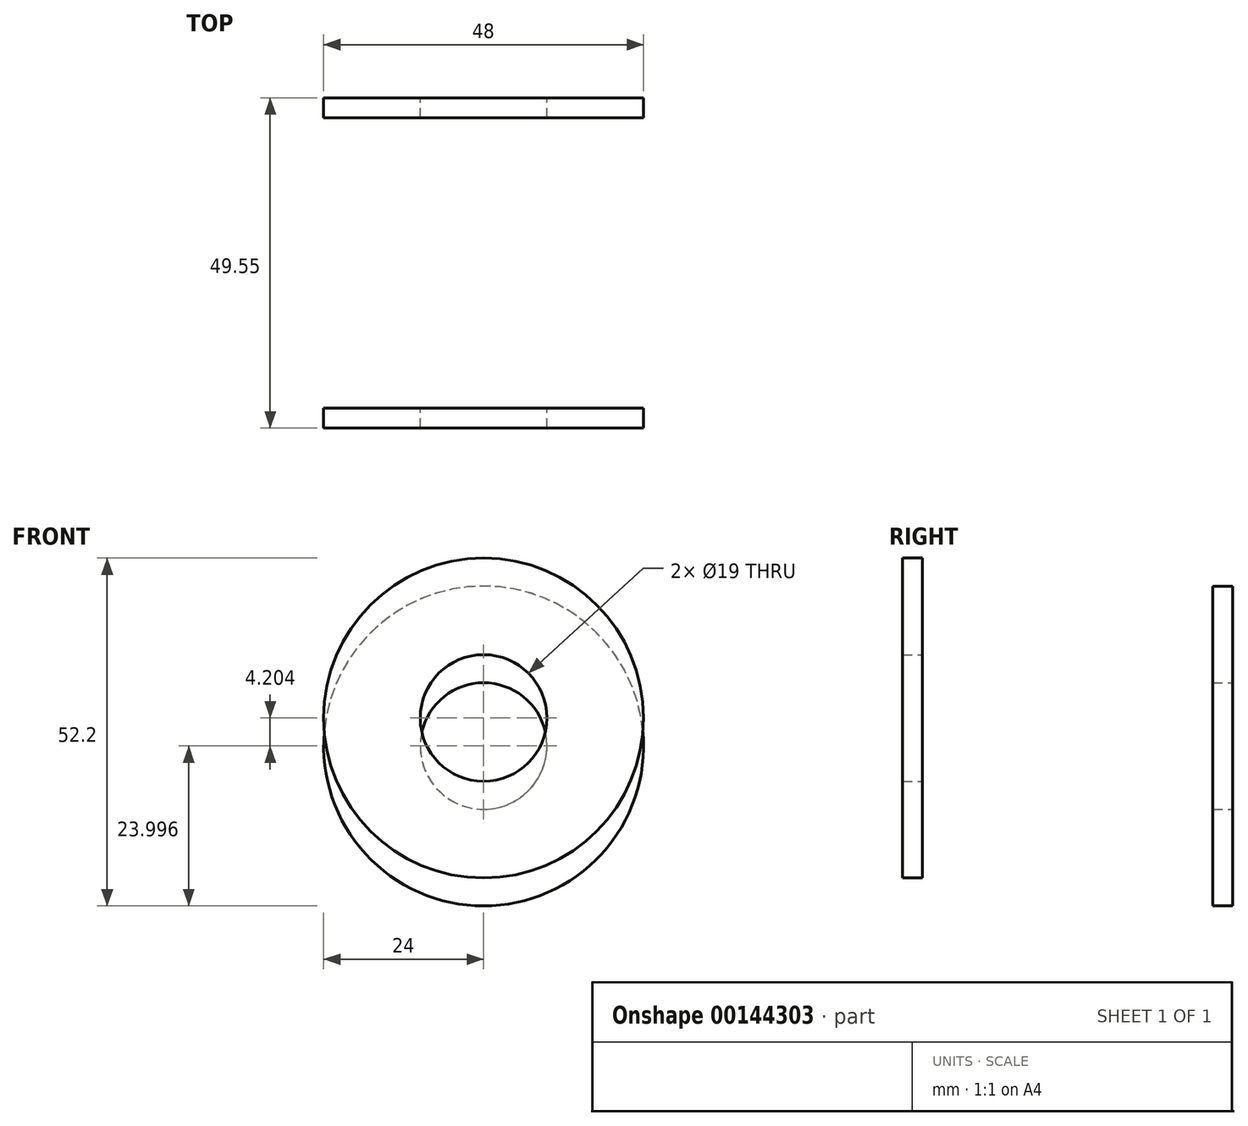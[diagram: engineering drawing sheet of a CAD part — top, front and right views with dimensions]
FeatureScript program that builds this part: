
annotation { "Feature Type Name" : "Feature", "Feature Type Description" : "" }
export const myFeature = defineFeature(function(context is Context, id is Id, definition is map)
    precondition{}
    {
        {
            var Q0;
            Q0=qCreatedBy(makeId("Front.planeOp"),FACE);
            var sketch = newSketch(context, id + "F0", { "sketchPlane" : qUnion([Q0])});
            skCircle(sketch, "E0", {"center": v(0, 0) * mm, "radius": 24 * mm});
            skCircle(sketch, "E1", {"center": v(0, 0) * mm, "radius": 9.5 * mm});
            skSolve(sketch);
        }
        {
            var Q0;
            Q0 = qSketchRegion(id + "F0", true);
            extrude(context, id + "F1", {"entities" : qUnion([Q0]), "depth" : 3 * mm});
        }
        {
            var Q0;
            Q0=makeQuery(id+"F1.opExtrude","SWEPT_BODY",BODY,{"disambiguationData":[OSD([sQuery(id+"F0.wireOp",EDGE,"E0"),sQuery(id+"F0.wireOp",EDGE,"E1")])]});
            transform(context, id + "F2", {"entities" : qUnion([Q0]), "transformType" : TransformType.TRANSLATION_3D, "dx" : 0 * mm, "dy" : 0 * mm, "dz" : 0 * mm, "makeCopy" : true});
        }
        {
            var Q0;
            Q0=makeQuery(id+"F2.opPattern","COPY",BODY,{"derivedFrom":makeQuery(id+"F1.opExtrude","SWEPT_BODY",BODY,{"disambiguationData":[OSD([sQuery(id+"F0.wireOp",EDGE,"E0"),sQuery(id+"F0.wireOp",EDGE,"E1")])]}),"instanceName":"1"});
            deleteBodies(context, id + "F3", {"entities" : qUnion([Q0])});
        }
        {
            var Q0;
            Q0=makeQuery(id+"F1.opExtrude","SWEPT_BODY",BODY,{"disambiguationData":[OSD([sQuery(id+"F0.wireOp",EDGE,"E0"),sQuery(id+"F0.wireOp",EDGE,"E1")])]});
            transform(context, id + "F4", {"entities" : qUnion([Q0]), "transformType" : TransformType.TRANSLATION_3D, "dx" : 0 * mm, "dy" : 46.55 * mm, "dz" : -4.2 * mm, "makeCopy" : true});
        }
    });
